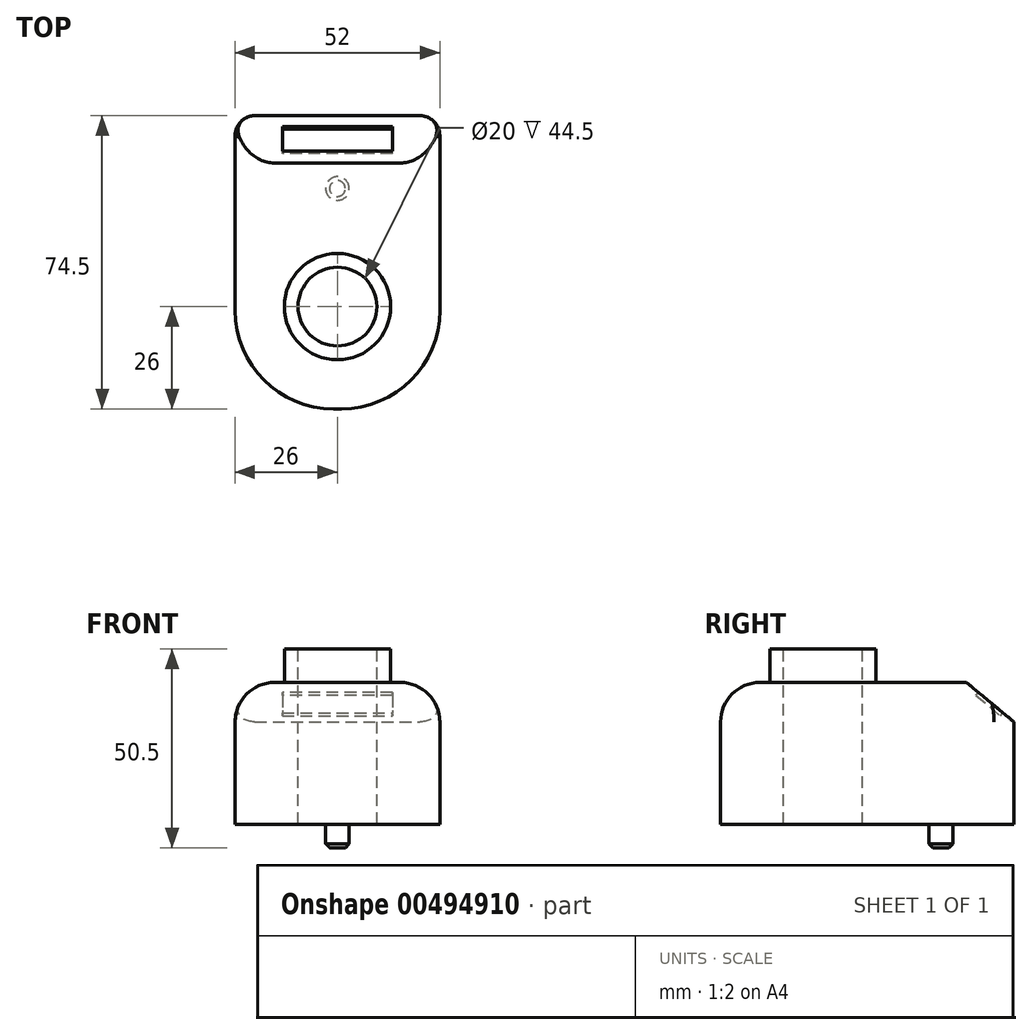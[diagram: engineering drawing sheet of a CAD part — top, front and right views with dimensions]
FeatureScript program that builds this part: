
annotation { "Feature Type Name" : "Feature", "Feature Type Description" : "" }
export const myFeature = defineFeature(function(context is Context, id is Id, definition is map)
    precondition{}
    {
        {
            var Q0;
            Q0=qCreatedBy(makeId("Top.planeOp"),FACE);
            var sketch = newSketch(context, id + "F0", { "sketchPlane" : qUnion([Q0])});
            skLineSegment(sketch, "E0.bottom", {"start": v(-21, 48.5) * mm, "end": v(21, 48.5) * mm});
            skLineSegment(sketch, "E0.top", {"start": v(-1, -26) * mm, "end": v(1, -26) * mm});
            skLineSegment(sketch, "E0.left", {"start": v(-26, 43.5) * mm, "end": v(-26, -1) * mm});
            skLineSegment(sketch, "E0.right", {"start": v(26, 43.5) * mm, "end": v(26, -1) * mm});
            skPoint(sketch, "E1.visualSharp", {"position": v(26, -26) * mm});
            skArc(sketch, "E1.filletArc", {"start": v(1, -26) * mm, "mid": v(18.68, -18.68) * mm, "end": v(26, -1) * mm});
            skPoint(sketch, "E2.visualSharp", {"position": v(-26, -26) * mm});
            skArc(sketch, "E2.filletArc", {"start": v(-26, -1) * mm, "mid": v(-18.68, -18.68) * mm, "end": v(-1, -26) * mm});
            skPoint(sketch, "E3.visualSharp", {"position": v(-26, 48.5) * mm});
            skArc(sketch, "E3.filletArc", {"start": v(-21, 48.5) * mm, "mid": v(-24.54, 47.04) * mm, "end": v(-26, 43.5) * mm});
            skPoint(sketch, "E4.visualSharp", {"position": v(26, 48.5) * mm});
            skArc(sketch, "E4.filletArc", {"start": v(26, 43.5) * mm, "mid": v(24.54, 47.04) * mm, "end": v(21, 48.5) * mm});
            skSolve(sketch);
        }
        {
            var Q0;
            Q0=qSketchRegion(id+"F0",true);
            extrude(context, id + "F1", {"entities" : qUnion([Q0]), "depth" : 36 * mm});
        }
        {
            var Q0;
            Q0=makeQuery(id+"F1.opExtrude","CAP_FACE",FACE,{"disambiguationData":[OSD([sQuery(id+"F0.wireOp",EDGE,"E0.bottom"),sQuery(id+"F0.wireOp",EDGE,"E0.top"),sQuery(id+"F0.wireOp",EDGE,"E0.left"),sQuery(id+"F0.wireOp",EDGE,"E0.right"),sQuery(id+"F0.wireOp",EDGE,"fd0d11bd-dff4-4bd1-8a6e-3f7a9caa409b.filletArc"),sQuery(id+"F0.wireOp",EDGE,"fbee6ad7-83b1-42cc-97bf-5a30b2db599f.filletArc"),sQuery(id+"F0.wireOp",EDGE,"E1.filletArc"),sQuery(id+"F0.wireOp",EDGE,"E2.filletArc")])],"isStart":false});
            var sketch = newSketch(context, id + "F2", { "sketchPlane" : qUnion([Q0])});
            skCircle(sketch, "E5", {"center": v(0, 0) * mm, "radius": 13.5 * mm});
            skSolve(sketch);
        }
        {
            var Q0;
            Q0=qSketchRegion(id+"F2",true);
            extrude(context, id + "F3", {"entities" : qUnion([Q0]), "operationType" : NewBodyOperationType.ADD, "depth" : 8.5 * mm});
        }
        {
            var Q0;
            Q0=makeQuery(id+"F1.opExtrude","CAP_FACE",FACE,{"disambiguationData":[OSD([sQuery(id+"F0.wireOp",EDGE,"E0.bottom"),sQuery(id+"F0.wireOp",EDGE,"E0.top"),sQuery(id+"F0.wireOp",EDGE,"E0.left"),sQuery(id+"F0.wireOp",EDGE,"E0.right"),sQuery(id+"F0.wireOp",EDGE,"fd0d11bd-dff4-4bd1-8a6e-3f7a9caa409b.filletArc"),sQuery(id+"F0.wireOp",EDGE,"fbee6ad7-83b1-42cc-97bf-5a30b2db599f.filletArc"),sQuery(id+"F0.wireOp",EDGE,"E1.filletArc"),sQuery(id+"F0.wireOp",EDGE,"E2.filletArc")])],"isStart":true});
            var sketch = newSketch(context, id + "F4", { "sketchPlane" : qUnion([Q0])});
            skCircle(sketch, "E6", {"center": v(0, -30) * mm, "radius": 3 * mm});
            skSolve(sketch);
        }
        {
            var Q0;
            Q0=qSketchRegion(id+"F4",true);
            extrude(context, id + "F5", {"entities" : qUnion([Q0]), "operationType" : NewBodyOperationType.ADD, "depth" : 6 * mm});
        }
        {
            var Q0;
            Q0=makeQuery(id+"F5.opExtrude","CAP_EDGE",EDGE,{"disambiguationData":[OSD([sQuery(id+"F4.wireOp",EDGE,"E6")])],"isStart":false});
            chamfer(context, id + "F6", {"entities" : qUnion([Q0]), "width" : 1 * mm, "tangentPropagation" : true});
        }
        {
            var Q0;
            Q0=makeQuery(id+"F1.opExtrude","CAP_EDGE",EDGE,{"disambiguationData":[OSD([sQuery(id+"F0.wireOp",EDGE,"E0.left")])],"isStart":false});
            var Q1;
            Q1=makeQuery(id+"F1.opExtrude","CAP_EDGE",EDGE,{"disambiguationData":[OSD([sQuery(id+"F0.wireOp",EDGE,"E0.bottom")])],"isStart":false});
            fillet(context, id + "F7", {"entities" : qUnion([Q0, Q1]), "radius" : 10 * mm, "tangentPropagation" : true, "allowEdgeOverflow" : false});
        }
        {
            var Q0;
            Q0=qCreatedBy(makeId("Right.planeOp"),FACE);
            var sketch = newSketch(context, id + "F8", { "sketchPlane" : qUnion([Q0])});
            skLineSegment(sketch, "E7", {"start": v(48.5, 36) * mm, "end": v(48.5, 26) * mm});
            skLineSegment(sketch, "E8", {"start": v(48.5, 36) * mm, "end": v(36.5, 36) * mm});
            skLineSegment(sketch, "E9", {"start": v(36.5, 36) * mm, "end": v(48.5, 26) * mm});
            skSolve(sketch);
        }
        {
            var Q0;
            Q0=qSketchRegion(id+"F8",true);
            extrude(context, id + "F9", {"entities" : qUnion([Q0]), "operationType" : NewBodyOperationType.REMOVE, "endBound" : BoundingType.THROUGH_ALL, "oppositeDirection" : true, "depth" : 25 * mm, "hasSecondDirection" : true, "secondDirectionBound" : BoundingType.THROUGH_ALL, "secondDirectionOppositeDirection" : false, "secondDirectionDepth" : 25 * mm});
        }
        {
            var Q0;
            Q0=makeQuery(id+"F9.boolean.opBoolean","COPY",FACE,{"derivedFrom":makeQuery(id+"F9.opExtrude","SWEPT_FACE",FACE,{"disambiguationData":[OSD([sQuery(id+"F8.wireOp",EDGE,"E9")])]})});
            var sketch = newSketch(context, id + "F10", { "sketchPlane" : qUnion([Q0])});
            skLineSegment(sketch, "E10", {"start": v(14, 9) * mm, "end": v(-14, 9) * mm});
            skLineSegment(sketch, "E11", {"start": v(-14, 9) * mm, "end": v(-14, 17) * mm});
            skLineSegment(sketch, "E12", {"start": v(-14, 17) * mm, "end": v(14, 17) * mm});
            skLineSegment(sketch, "E13", {"start": v(14, 9) * mm, "end": v(14, 17) * mm});
            skSolve(sketch);
        }
        {
            var Q0;
            Q0=qSketchRegion(id+"F10",true);
            extrude(context, id + "F11", {"entities" : qUnion([Q0]), "operationType" : NewBodyOperationType.REMOVE, "oppositeDirection" : true, "depth" : 1 * mm});
        }
        {
            var Q0;
            Q0=makeQuery(id+"F3.opExtrude","CAP_FACE",FACE,{"disambiguationData":[OSD([sQuery(id+"F2.wireOp",EDGE,"E5")])],"isStart":false});
            var sketch = newSketch(context, id + "F12", { "sketchPlane" : qUnion([Q0])});
            skCircle(sketch, "E14", {"center": v(0, 0) * mm, "radius": 10 * mm});
            skSolve(sketch);
        }
        {
            var Q0;
            Q0=qSketchRegion(id+"F12",true);
            extrude(context, id + "F13", {"entities" : qUnion([Q0]), "operationType" : NewBodyOperationType.REMOVE, "endBound" : BoundingType.THROUGH_ALL, "oppositeDirection" : true, "depth" : 25 * mm});
        }
    });
